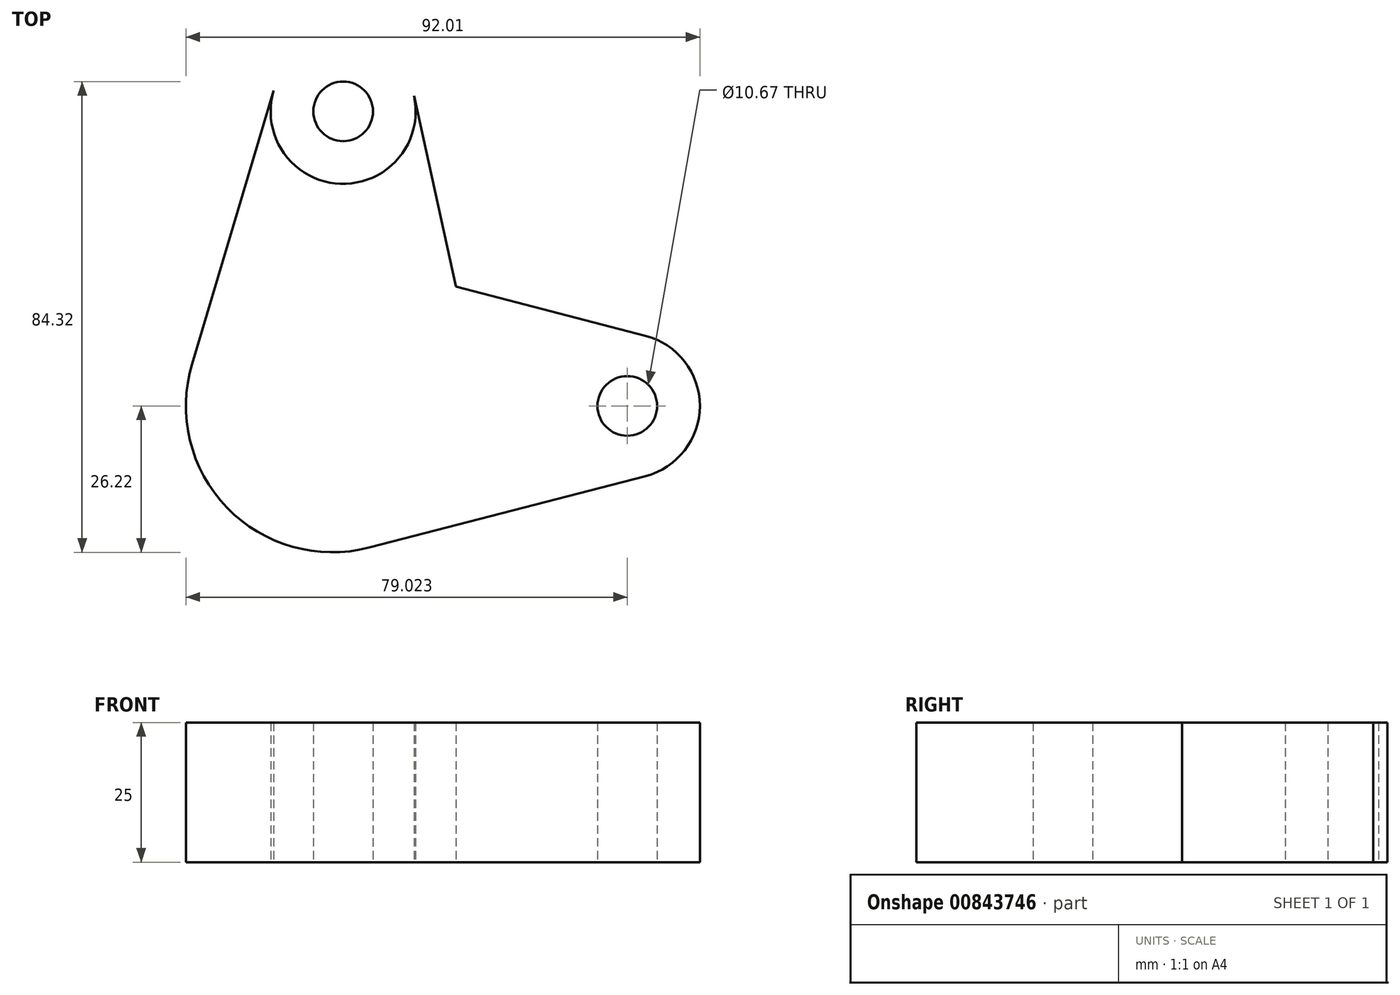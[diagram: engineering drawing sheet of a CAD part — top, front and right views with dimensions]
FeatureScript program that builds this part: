
annotation { "Feature Type Name" : "Feature", "Feature Type Description" : "" }
export const myFeature = defineFeature(function(context is Context, id is Id, definition is map)
    precondition{}
    {
        {
            var Q0;
            Q0=qCreatedBy(makeId("Top.planeOp"),FACE);
            var sketch = newSketch(context, id + "F0", { "sketchPlane" : qUnion([Q0])});
            skCircle(sketch, "E0", {"center": v(0, 0) * mm, "radius": 26.22 * mm});
            skCircle(sketch, "E1", {"center": v(52.8, 0) * mm, "radius": 12.98 * mm});
            skCircle(sketch, "E2", {"center": v(52.8, 0) * mm, "radius": 5.34 * mm});
            skLineSegment(sketch, "E3", {"start": v(6.57, 25.38) * mm, "end": v(56.06, 12.57) * mm});
            skLineSegment(sketch, "E4.MirrorCS", {"start": v(6.57, -25.38) * mm, "end": v(56.06, -12.57) * mm});
            skLineSegment(sketch, "E5.MirrorCS", {"start": v(25.6, 5.64) * mm, "end": v(14.61, 55.56) * mm});
            skLineSegment(sketch, "E6.MirrorCS", {"start": v(-25.12, 7.5) * mm, "end": v(-10.5, 56.48) * mm});
            skCircle(sketch, "E7.MirrorC", {"center": v(1.93, 52.77) * mm, "radius": 12.98 * mm});
            skCircle(sketch, "E8.MirrorC", {"center": v(1.93, 52.77) * mm, "radius": 5.34 * mm});
            skSolve(sketch);
        }
        {
            var Q0;
            Q0=makeQuery(id+"F0.imprint","IMPRINT",FACE,{"disambiguationData":[TD([[makeQuery(id+"F0.imprint","IMPRINT",EDGE,{"derivedFrom":sQuery(id+"F0.wireOp",EDGE,"E8.MirrorC")}),1.0]])]});
            var Q1;
            {var subQ0=sQuery(id+"F0.wireOp",EDGE,"E6.MirrorCS");Q1=makeQuery(id+"F0.imprint","IMPRINT",FACE,{"disambiguationData":[TD([[makeQuery(id+"F0.imprint","IMPRINT",EDGE,{"derivedFrom":subQ0}),-1.0]])]});}
            var Q2;
            {var subQ0=sQuery(id+"F0.wireOp",EDGE,"E3");var subQ1=sQuery(id+"F0.wireOp",EDGE,"E0");var subQ2=makeQuery(id+"F0.imprint","INTERSECT",VERTEX,{"derivedFrom":[subQ1,subQ0]});Q2=makeQuery(id+"F0.imprint","IMPRINT",FACE,{"disambiguationData":[TD([[makeQuery(id+"F0.imprint","IMPRINT",EDGE,{"disambiguationData":[TD([[subQ2,1.0]])],"derivedFrom":subQ1}),-1.0]])]});}
            var Q3;
            {var subQ0=sQuery(id+"F0.wireOp",EDGE,"E0");var subQ1=makeQuery(id+"F0.imprint","INTERSECT",VERTEX,{"derivedFrom":[subQ0,sQuery(id+"F0.wireOp",EDGE,"E3")]});Q3=makeQuery(id+"F0.imprint","IMPRINT",FACE,{"disambiguationData":[TD([[makeQuery(id+"F0.imprint","IMPRINT",EDGE,{"disambiguationData":[TD([[subQ1,1.0]])],"derivedFrom":subQ0}),1.0]])]});}
            var Q4;
            Q4=makeQuery(id+"F0.imprint","IMPRINT",FACE,{"disambiguationData":[TD([[makeQuery(id+"F0.imprint","IMPRINT",EDGE,{"derivedFrom":sQuery(id+"F0.wireOp",EDGE,"E2")}),-1.0]])]});
            var Q5;
            {var subQ0=sQuery(id+"F0.wireOp",EDGE,"E4.MirrorCS");Q5=makeQuery(id+"F0.imprint","IMPRINT",FACE,{"disambiguationData":[TD([[makeQuery(id+"F0.imprint","IMPRINT",EDGE,{"derivedFrom":subQ0}),1.0]])]});}
            extrude(context, id + "F1", {"entities" : qUnion([Q0, Q1, Q2, Q3, Q4, Q5]), "depth" : 25 * mm, "offsetDistance" : 25 * mm});
        }
    });
